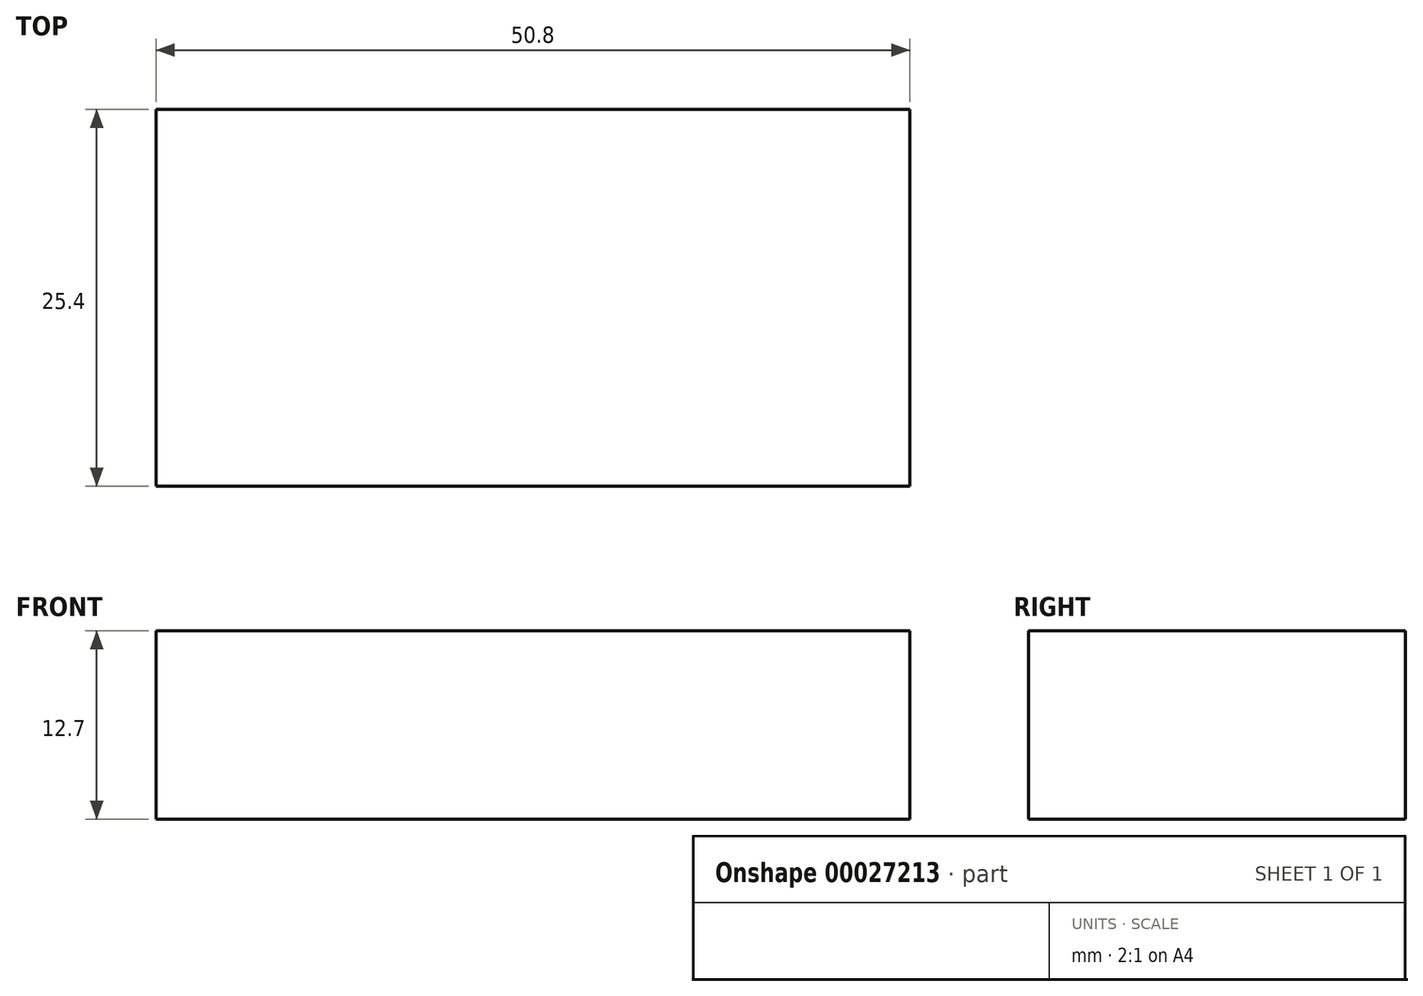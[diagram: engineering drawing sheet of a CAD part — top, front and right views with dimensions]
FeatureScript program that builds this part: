
annotation { "Feature Type Name" : "Feature", "Feature Type Description" : "" }
export const myFeature = defineFeature(function(context is Context, id is Id, definition is map)
    precondition{}
    {
        {
            var Q0;
            Q0=qCreatedBy(makeId("Front.planeOp"),FACE);
            var sketch = newSketch(context, id + "F0", { "sketchPlane" : qUnion([Q0])});
            skLineSegment(sketch, "E0.bottom", {"start": v(0, 0) * mm, "end": v(50.8, 0) * mm});
            skLineSegment(sketch, "E0.top", {"start": v(0, 12.7) * mm, "end": v(50.8, 12.7) * mm});
            skLineSegment(sketch, "E0.left", {"start": v(0, 0) * mm, "end": v(0, 12.7) * mm});
            skLineSegment(sketch, "E0.right", {"start": v(50.8, 0) * mm, "end": v(50.8, 12.7) * mm});
            skSolve(sketch);
        }
        {
            var Q0;
            Q0=makeQuery(id+"F0.imprint","IMPRINT",FACE,{"disambiguationData":[TD([[makeQuery(id+"F0.imprint","IMPRINT",EDGE,{"derivedFrom":sQuery(id+"F0.wireOp",EDGE,"E0.bottom")}),1.0]])]});
            extrude(context, id + "F1", {"entities" : qUnion([Q0]), "depth" : 25.4 * mm});
        }
    });
